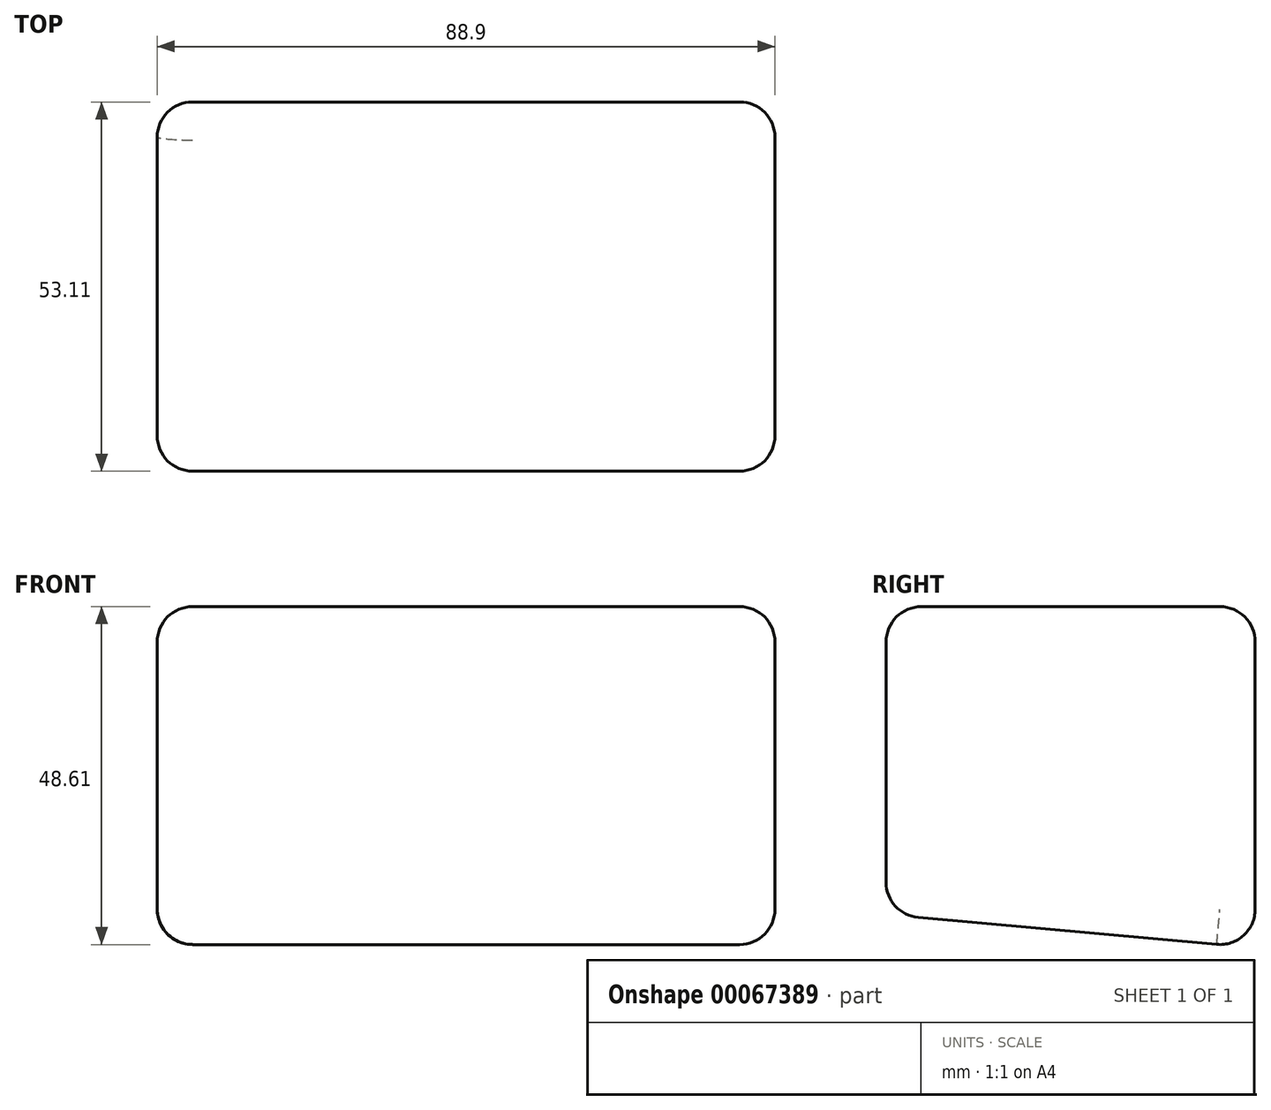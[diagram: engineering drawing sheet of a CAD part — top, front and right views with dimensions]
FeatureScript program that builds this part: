
annotation { "Feature Type Name" : "Feature", "Feature Type Description" : "" }
export const myFeature = defineFeature(function(context is Context, id is Id, definition is map)
    precondition{}
    {
        {
            var Q0;
            Q0=qCreatedBy(makeId("Right.planeOp"),FACE);
            var sketch = newSketch(context, id + "F0", { "sketchPlane" : qUnion([Q0])});
            skLineSegment(sketch, "E0", {"start": v(-33.44, 30.92) * mm, "end": v(19.67, 30.92) * mm});
            skLineSegment(sketch, "E1", {"start": v(19.67, 30.92) * mm, "end": v(19.67, -18.17) * mm});
            skLineSegment(sketch, "E2", {"start": v(19.67, -18.17) * mm, "end": v(-33.44, -13.38) * mm});
            skLineSegment(sketch, "E3", {"start": v(-33.44, -13.38) * mm, "end": v(-33.44, 30.92) * mm});
            skSolve(sketch);
        }
        {
            var Q0;
            Q0=makeQuery(id+"F0.imprint","IMPRINT",FACE,{"disambiguationData":[TD([[makeQuery(id+"F0.imprint","IMPRINT",EDGE,{"derivedFrom":sQuery(id+"F0.wireOp",EDGE,"E0")}),-1.0]])]});
            extrude(context, id + "F1", {"entities" : qUnion([Q0]), "endBound" : BoundingType.SYMMETRIC, "depth" : 88.9 * mm, "hasDraft" : true, "draftAngle" : 0 * degree});
        }
        {
            var Q0;
            {var subQ0=makeQuery(id+"F1.opExtrude","SWEPT_EDGE",EDGE,{"disambiguationData":[OSD([sQuery(id+"F0.wireOp",EDGE,"E0"),sQuery(id+"F0.wireOp",EDGE,"E3")])]});Q0=makeQuery(id+"F1.booleanUnion0.opBoolean","MERGE",EDGE,{"derivedFrom":[makeQuery(id+"F1.split0.splitOp","SPLIT",EDGE,{"derivedFrom":subQ0,"isFromBackBody":true}),makeQuery(id+"F1.split0.splitOp","SPLIT",EDGE,{"derivedFrom":subQ0})]});}
            var Q1;
            {var subQ0=makeQuery(id+"F1.opExtrude","SWEPT_EDGE",EDGE,{"disambiguationData":[OSD([sQuery(id+"F0.wireOp",EDGE,"E0"),sQuery(id+"F0.wireOp",EDGE,"E1")])]});Q1=makeQuery(id+"F1.booleanUnion0.opBoolean","MERGE",EDGE,{"derivedFrom":[makeQuery(id+"F1.split0.splitOp","SPLIT",EDGE,{"derivedFrom":subQ0,"isFromBackBody":true}),makeQuery(id+"F1.split0.splitOp","SPLIT",EDGE,{"derivedFrom":subQ0})]});}
            var Q2;
            Q2=makeQuery(id+"F1.opExtrude","CAP_EDGE",EDGE,{"disambiguationData":[OSD([sQuery(id+"F0.wireOp",EDGE,"E0")])],"isStart":false});
            var Q3;
            Q3=makeQuery(id+"F1.opExtrude","CAP_EDGE",EDGE,{"disambiguationData":[OSD([sQuery(id+"F0.wireOp",EDGE,"E3")])],"isStart":false});
            var Q4;
            {var subQ0=makeQuery(id+"F1.opExtrude","SWEPT_EDGE",EDGE,{"disambiguationData":[OSD([sQuery(id+"F0.wireOp",EDGE,"E2"),sQuery(id+"F0.wireOp",EDGE,"E3")])]});Q4=makeQuery(id+"F1.booleanUnion0.opBoolean","MERGE",EDGE,{"derivedFrom":[makeQuery(id+"F1.split0.splitOp","SPLIT",EDGE,{"derivedFrom":subQ0,"isFromBackBody":true}),makeQuery(id+"F1.split0.splitOp","SPLIT",EDGE,{"derivedFrom":subQ0})]});}
            var Q5;
            Q5=makeQuery(id+"F1.opExtrude","CAP_EDGE",EDGE,{"disambiguationData":[OSD([sQuery(id+"F0.wireOp",EDGE,"E2")])],"isStart":false});
            var Q6;
            Q6=makeQuery(id+"F1.opExtrude","CAP_EDGE",EDGE,{"disambiguationData":[OSD([sQuery(id+"F0.wireOp",EDGE,"E1")])],"isStart":false});
            var Q7;
            Q7=makeQuery(id+"F1.opExtrude","CAP_EDGE",EDGE,{"disambiguationData":[OSD([sQuery(id+"F0.wireOp",EDGE,"E0")])],"isStart":true});
            var Q8;
            Q8=makeQuery(id+"F1.opExtrude","CAP_EDGE",EDGE,{"disambiguationData":[OSD([sQuery(id+"F0.wireOp",EDGE,"E3")])],"isStart":true});
            var Q9;
            {var subQ0=makeQuery(id+"F1.opExtrude","SWEPT_EDGE",EDGE,{"disambiguationData":[OSD([sQuery(id+"F0.wireOp",EDGE,"E1"),sQuery(id+"F0.wireOp",EDGE,"E2")])]});Q9=makeQuery(id+"F1.booleanUnion0.opBoolean","MERGE",EDGE,{"derivedFrom":[makeQuery(id+"F1.split0.splitOp","SPLIT",EDGE,{"derivedFrom":subQ0,"isFromBackBody":true}),makeQuery(id+"F1.split0.splitOp","SPLIT",EDGE,{"derivedFrom":subQ0})]});}
            var Q10;
            Q10=makeQuery(id+"F1.opExtrude","CAP_EDGE",EDGE,{"disambiguationData":[OSD([sQuery(id+"F0.wireOp",EDGE,"E2")])],"isStart":true});
            fillet(context, id + "F2", {"entities" : qUnion([Q0, Q1, Q2, Q3, Q4, Q5, Q6, Q7, Q8, Q9, Q10]), "radius" : 5.08 * mm, "tangentPropagation" : true, "allowEdgeOverflow" : false});
        }
        {
            var Q0;
            Q0=makeQuery(id+"F1.opExtrude","CAP_EDGE",EDGE,{"disambiguationData":[OSD([sQuery(id+"F0.wireOp",EDGE,"E1")])],"isStart":true});
            fillet(context, id + "F3", {"entities" : qUnion([Q0]), "radius" : 5.08 * mm, "tangentPropagation" : true, "allowEdgeOverflow" : false});
        }
    });
